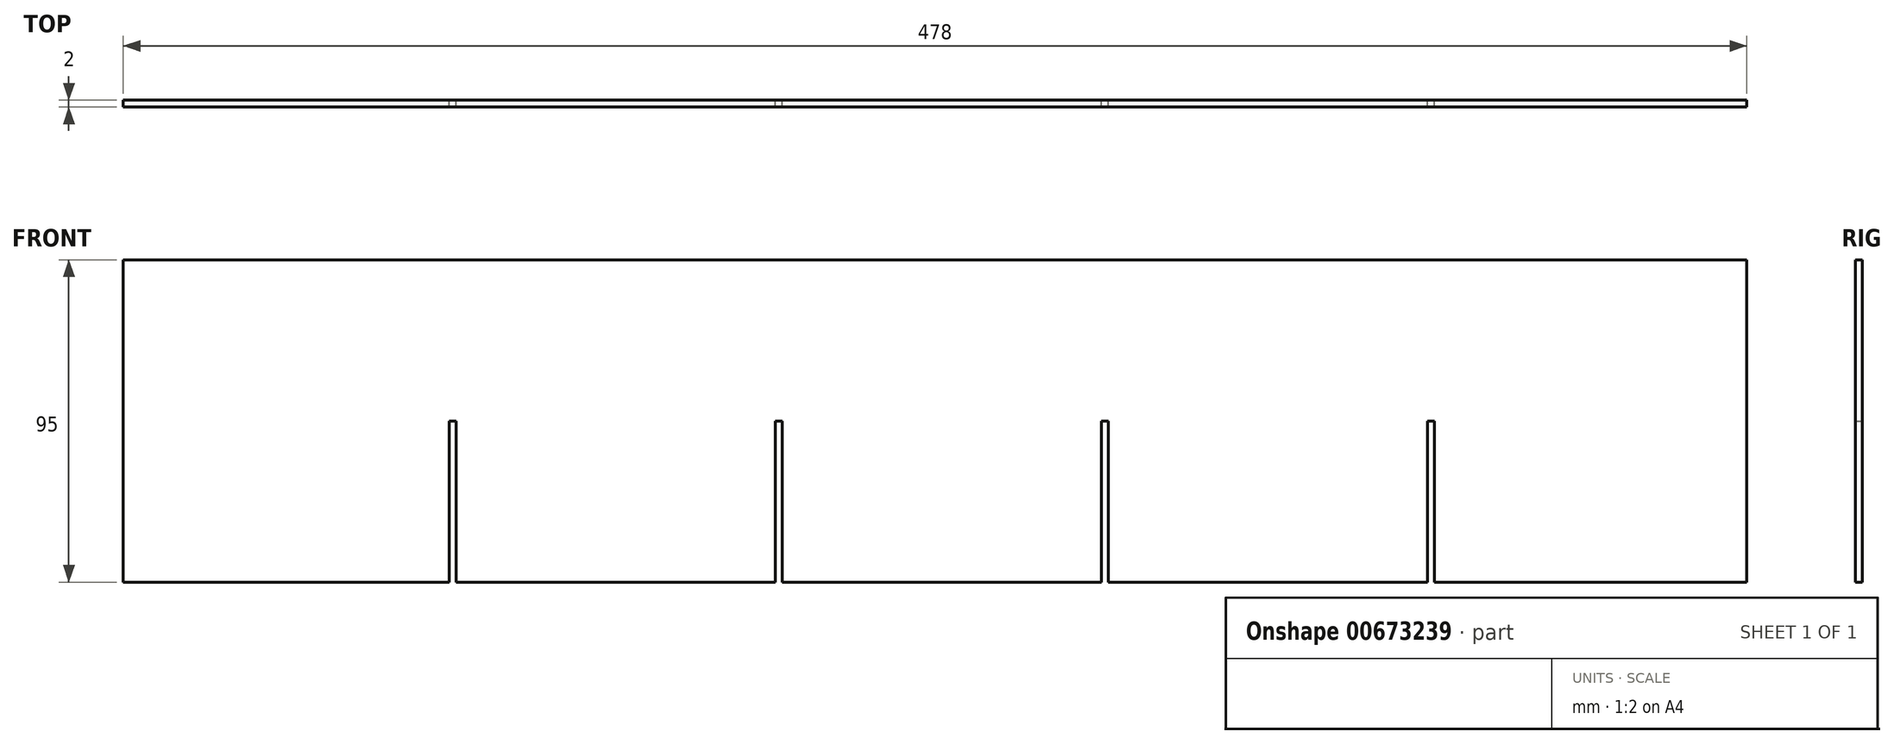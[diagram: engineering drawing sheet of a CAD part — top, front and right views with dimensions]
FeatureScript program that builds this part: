
annotation { "Feature Type Name" : "Feature", "Feature Type Description" : "" }
export const myFeature = defineFeature(function(context is Context, id is Id, definition is map)
    precondition{}
    {
        {
            var Q0;
            Q0=qCreatedBy(makeId("Front.planeOp"),FACE);
            var sketch = newSketch(context, id + "F0", { "sketchPlane" : qUnion([Q0])});
            skLineSegment(sketch, "E0.bottom", {"start": v(-239, -47.5) * mm, "end": v(-143, -47.5) * mm});
            skLineSegment(sketch, "E0.top", {"start": v(-239, 47.5) * mm, "end": v(239, 47.5) * mm});
            skLineSegment(sketch, "E0.left", {"start": v(-239, -47.5) * mm, "end": v(-239, 47.5) * mm});
            skLineSegment(sketch, "E0.right", {"start": v(239, -47.5) * mm, "end": v(239, 47.5) * mm});
            skPoint(sketch, "E0.middle", {"position": v(0, 0) * mm});
            skLineSegment(sketch, "E1", {"start": v(-143, -47.5) * mm, "end": v(-143, 0) * mm});
            skLineSegment(sketch, "E2", {"start": v(-143, 0) * mm, "end": v(-141, 0) * mm});
            skLineSegment(sketch, "E3", {"start": v(-141, 0) * mm, "end": v(-141, -47.5) * mm});
            skLineSegment(sketch, "E4.1.0.0", {"start": v(-47, -47.5) * mm, "end": v(-47, 0) * mm});
            skLineSegment(sketch, "E4.1.0.1", {"start": v(-47, 0) * mm, "end": v(-45, 0) * mm});
            skLineSegment(sketch, "E4.1.0.2", {"start": v(-45, 0) * mm, "end": v(-45, -47.5) * mm});
            skLineSegment(sketch, "E4.2.0.0", {"start": v(49, -47.5) * mm, "end": v(49, 0) * mm});
            skLineSegment(sketch, "E4.2.0.1", {"start": v(49, 0) * mm, "end": v(51, 0) * mm});
            skLineSegment(sketch, "E4.2.0.2", {"start": v(51, 0) * mm, "end": v(51, -47.5) * mm});
            skLineSegment(sketch, "E4.3.0.0", {"start": v(145, -47.5) * mm, "end": v(145, 0) * mm});
            skLineSegment(sketch, "E4.3.0.1", {"start": v(145, 0) * mm, "end": v(147, 0) * mm});
            skLineSegment(sketch, "E4.3.0.2", {"start": v(147, 0) * mm, "end": v(147, -47.5) * mm});
            skLineSegment(sketch, "E4.direction1", {"start": v(-141, -47.5) * mm, "end": v(-47, -47.5) * mm, "construction": true});
            skLineSegment(sketch, "E5.trimOffspring", {"start": v(-141, -47.5) * mm, "end": v(-47, -47.5) * mm});
            skLineSegment(sketch, "E6.trimOffspring", {"start": v(-45, -47.5) * mm, "end": v(49, -47.5) * mm});
            skLineSegment(sketch, "E7.trimOffspring", {"start": v(51, -47.5) * mm, "end": v(145, -47.5) * mm});
            skLineSegment(sketch, "E8.trimOffspring", {"start": v(147, -47.5) * mm, "end": v(239, -47.5) * mm});
            skSolve(sketch);
        }
        {
            var Q0;
            Q0=makeQuery(id+"F0.imprint","IMPRINT",FACE,{"disambiguationData":[TD([[makeQuery(id+"F0.imprint","IMPRINT",EDGE,{"derivedFrom":sQuery(id+"F0.wireOp",EDGE,"E0.bottom")}),1.0]])]});
            extrude(context, id + "F1", {"entities" : qUnion([Q0]), "endBound" : BoundingType.SYMMETRIC, "depth" : 2 * mm, "offsetDistance" : 25 * mm});
        }
    });
